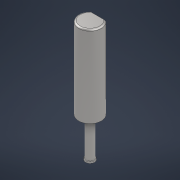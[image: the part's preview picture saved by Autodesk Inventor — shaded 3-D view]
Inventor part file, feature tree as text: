
AUTODESK INVENTOR PART (.ipt)
format: ipt  version: 2021 (Build 250183000, 183)  size: 121,344 bytes
history: native  units: mm
features: extrude x4, sketch x4, other x2, fillet x1
ambient origin geometry x8: Origin, YZ Plane, XZ Plane, XY Plane, X Axis, Y Axis, Z Axis, Center Point
bodies: Body1 (feature_tree)
feature tree (11):
  other  "Eixo - Encaixe D"
  other  "Sólido1"
  extrude  "Extrusão1"  Depth=10.8mm TaperAngle=0.0deg
  extrude  "Extrusão2"  Depth=9.0mm TaperAngle=0.0deg
  extrude  "Extrusão3"  Depth=5.0mm TaperAngle=0.0deg
  extrude  "Extrusão4"  Depth=0.2mm TaperAngle=0.0deg
  fillet  "Arredondamento1"  Radius=0.2mm
  sketch  "Esboço1"  dims[d0=3.0mm d1=10.8mm d2=0.0mm]
  sketch  "Esboço2"  dims[d3=0.5mm d4=9.0mm d5=0.0mm]
  sketch  "Esboço3"  dims[d6=1.0mm d7=5.0mm d8=0.0mm]
  sketch  "Esboço4"  dims[d9=1.2mm d10=0.2mm d11=0.0mm d12=0.2mm]
